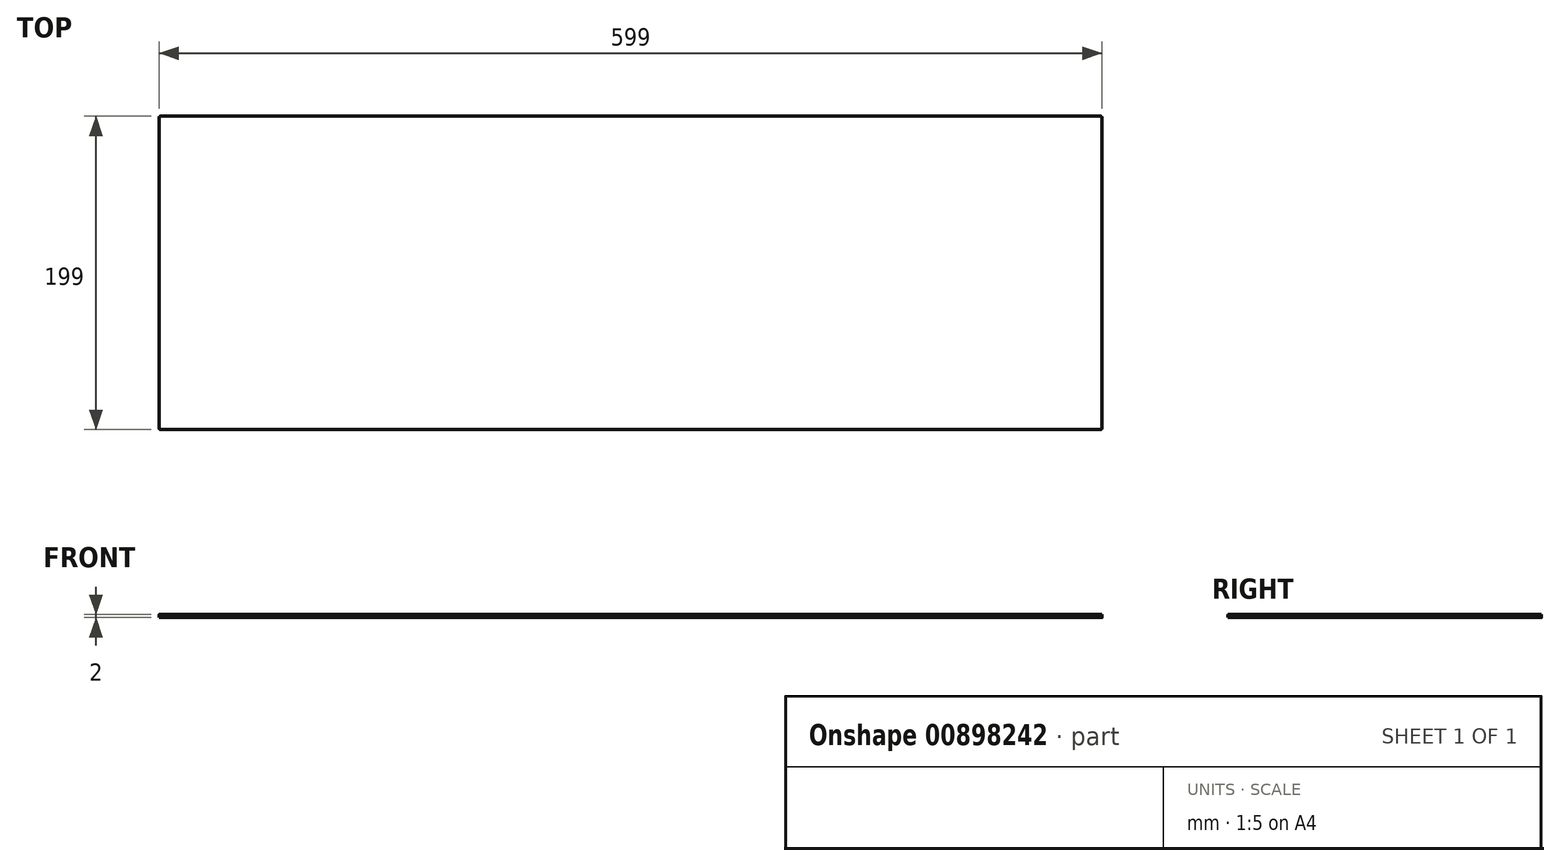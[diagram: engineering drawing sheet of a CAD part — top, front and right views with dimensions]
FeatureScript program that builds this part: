
annotation { "Feature Type Name" : "Feature", "Feature Type Description" : "" }
export const myFeature = defineFeature(function(context is Context, id is Id, definition is map)
    precondition{}
    {
        {
            var Q0;
            Q0=qCreatedBy(makeId("Top.planeOp"),FACE);
            var sketch = newSketch(context, id + "F0", { "sketchPlane" : qUnion([Q0])});
            skLineSegment(sketch, "E0.bottom", {"start": v(298.5, -99.5) * mm, "end": v(-298.5, -99.5) * mm});
            skLineSegment(sketch, "E0.top", {"start": v(298.5, 99.5) * mm, "end": v(-298.5, 99.5) * mm});
            skLineSegment(sketch, "E0.left", {"start": v(299.5, -98.5) * mm, "end": v(299.5, 98.5) * mm});
            skLineSegment(sketch, "E0.right", {"start": v(-299.5, -98.5) * mm, "end": v(-299.5, 98.5) * mm});
            skPoint(sketch, "E0.middle", {"position": v(0, 0) * mm});
            skPoint(sketch, "E1.visualSharp", {"position": v(-299.5, 99.5) * mm});
            skArc(sketch, "E1.filletArc", {"start": v(-298.5, 99.5) * mm, "mid": v(-299.2, 99.2) * mm, "end": v(-299.5, 98.5) * mm});
            skPoint(sketch, "E2.visualSharp", {"position": v(299.5, 99.5) * mm});
            skArc(sketch, "E2.filletArc", {"start": v(299.5, 98.5) * mm, "mid": v(299.2, 99.2) * mm, "end": v(298.5, 99.5) * mm});
            skPoint(sketch, "E3.visualSharp", {"position": v(-299.5, -99.5) * mm});
            skArc(sketch, "E3.filletArc", {"start": v(-299.5, -98.5) * mm, "mid": v(-299.2, -99.2) * mm, "end": v(-298.5, -99.5) * mm});
            skPoint(sketch, "E4.visualSharp", {"position": v(299.5, -99.5) * mm});
            skArc(sketch, "E4.filletArc", {"start": v(298.5, -99.5) * mm, "mid": v(299.2, -99.2) * mm, "end": v(299.5, -98.5) * mm});
            skSolve(sketch);
        }
        {
            var Q0;
            Q0=qSketchRegion(id+"F0",true);
            extrude(context, id + "F1", {"entities" : qUnion([Q0]), "oppositeDirection" : true, "depth" : 2 * mm});
        }
    });
